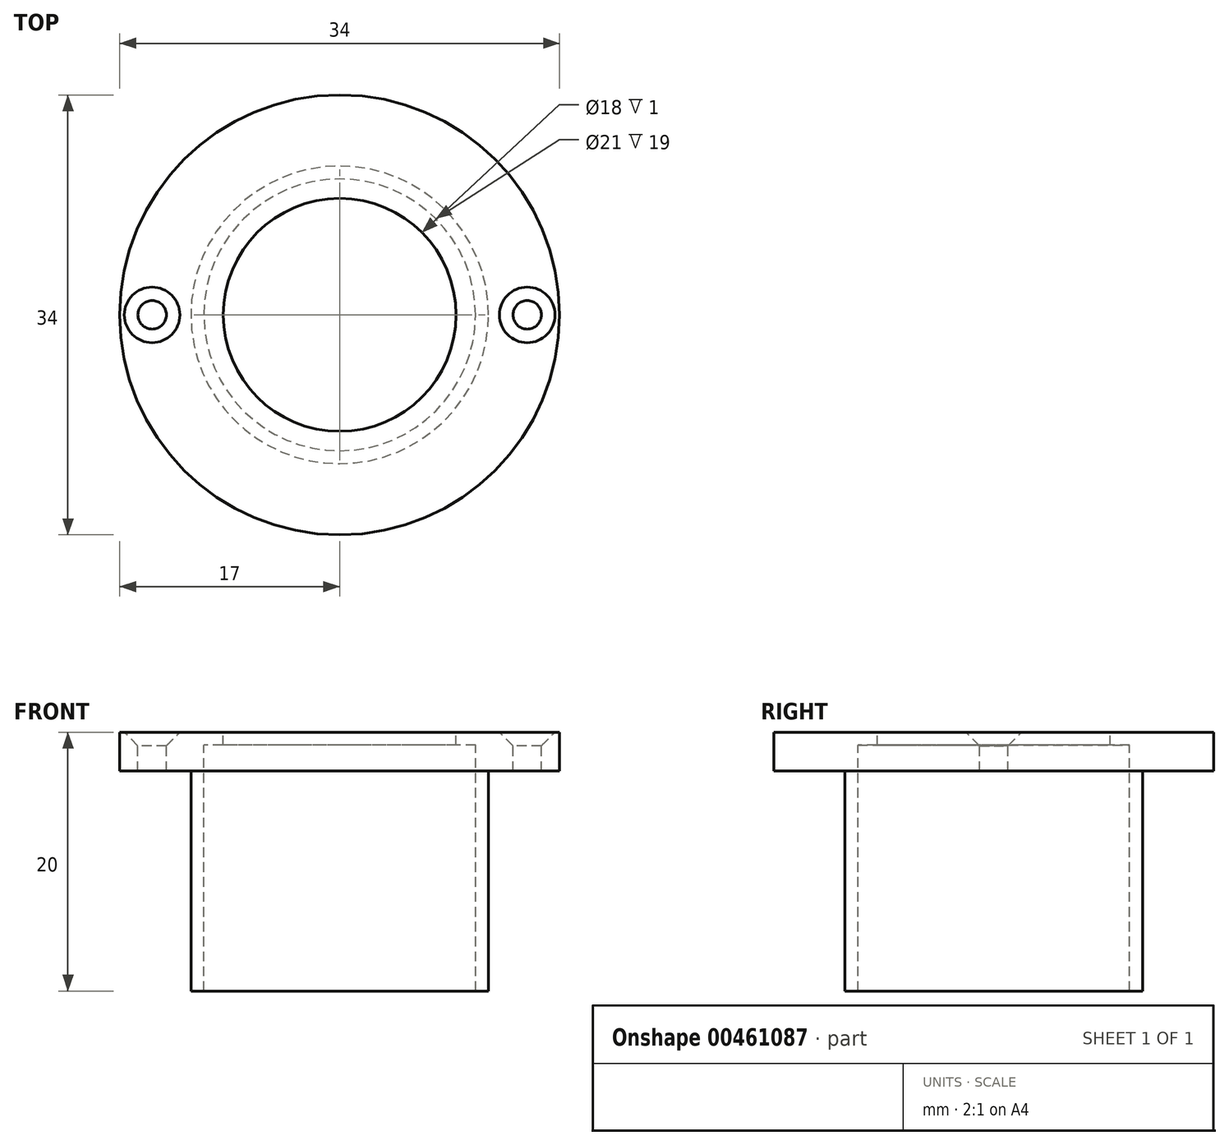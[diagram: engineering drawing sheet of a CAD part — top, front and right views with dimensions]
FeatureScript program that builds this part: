
annotation { "Feature Type Name" : "Feature", "Feature Type Description" : "" }
export const myFeature = defineFeature(function(context is Context, id is Id, definition is map)
    precondition{}
    {
        {
            var Q0;
            Q0=qCreatedBy(makeId("Front.planeOp"),FACE);
            var sketch = newSketch(context, id + "F0", { "sketchPlane" : qUnion([Q0])});
            skLineSegment(sketch, "E0", {"start": v(-9, 0) * mm, "end": v(-9, -1) * mm});
            skLineSegment(sketch, "E1", {"start": v(-9, -1) * mm, "end": v(-10.5, -1) * mm});
            skLineSegment(sketch, "E2", {"start": v(-10.5, -1) * mm, "end": v(-10.5, -20) * mm});
            skLineSegment(sketch, "E3", {"start": v(-10.5, -20) * mm, "end": v(-11.5, -20) * mm});
            skLineSegment(sketch, "E4", {"start": v(-11.5, -20) * mm, "end": v(-11.5, -3) * mm});
            skLineSegment(sketch, "E5", {"start": v(-11.5, -3) * mm, "end": v(-17, -3) * mm});
            skLineSegment(sketch, "E6", {"start": v(-17, 0) * mm, "end": v(-9, 0) * mm});
            skLineSegment(sketch, "E7", {"start": v(0, 0) * mm, "end": v(0, 0) * mm});
            skLineSegment(sketch, "E8", {"start": v(0, 5.59) * mm, "end": v(0, -47.58) * mm});
            skLineSegment(sketch, "E9", {"start": v(-17, -3) * mm, "end": v(-17, 0) * mm});
            skSolve(sketch);
        }
        {
            var Q0;
            Q0=makeQuery(id+"F0.imprint","IMPRINT",FACE,{"disambiguationData":[TD([[makeQuery(id+"F0.imprint","IMPRINT",EDGE,{"derivedFrom":sQuery(id+"F0.wireOp",EDGE,"E0")}),-1.0]])]});
            var Q1;
            Q1=sQuery(id+"F0.wireOp",EDGE,"E8");
            revolve(context, id + "F1", {"entities" : qUnion([Q0]), "axis" : qUnion([Q1]), "revolveType" : RevolveType.FULL});
        }
        {
            var Q0;
            Q0=qCreatedBy(makeId("Top.planeOp"),FACE);
            var sketch = newSketch(context, id + "F2", { "sketchPlane" : qUnion([Q0])});
            skPoint(sketch, "E10", {"position": v(-14.5, 0) * mm});
            skPoint(sketch, "E11", {"position": v(14.5, 0) * mm});
            skSolve(sketch);
        }
        {
            var Q0;
            Q0=sQuery(id+"F2.wireOp",VERTEX,"E10");
            var Q1;
            Q1=sQuery(id+"F2.wireOp",VERTEX,"E11");
            var Q2;
            Q2=makeQuery(id+"F1.opRevolve","SWEPT_BODY",BODY,{"disambiguationData":[OSD([sQuery(id+"F0.wireOp",EDGE,"E0"),sQuery(id+"F0.wireOp",EDGE,"E1"),sQuery(id+"F0.wireOp",EDGE,"E2"),sQuery(id+"F0.wireOp",EDGE,"E3"),sQuery(id+"F0.wireOp",EDGE,"E4"),sQuery(id+"F0.wireOp",EDGE,"E5"),sQuery(id+"F0.wireOp",EDGE,"jsLfDVp0-pqyE-hRxw-NHHF-bIH2GOawU8vu"),sQuery(id+"F0.wireOp",EDGE,"E6")])]});
            hole(context, id + "F3", {"style" : HoleStyle.C_SINK, "endStyle" : HoleEndStyle.THROUGH, "holeDiameter" : 2.2 * mm, "cSinkDiameter" : 4.3 * mm, "cSinkAngle" : 90 * degree, "isTappedThrough" : true, "tappedDepth" : 12 * mm, "tapClearance" : 3, "locations" : qUnion([Q0, Q1]), "scope" : qUnion([Q2])});
        }
    });
